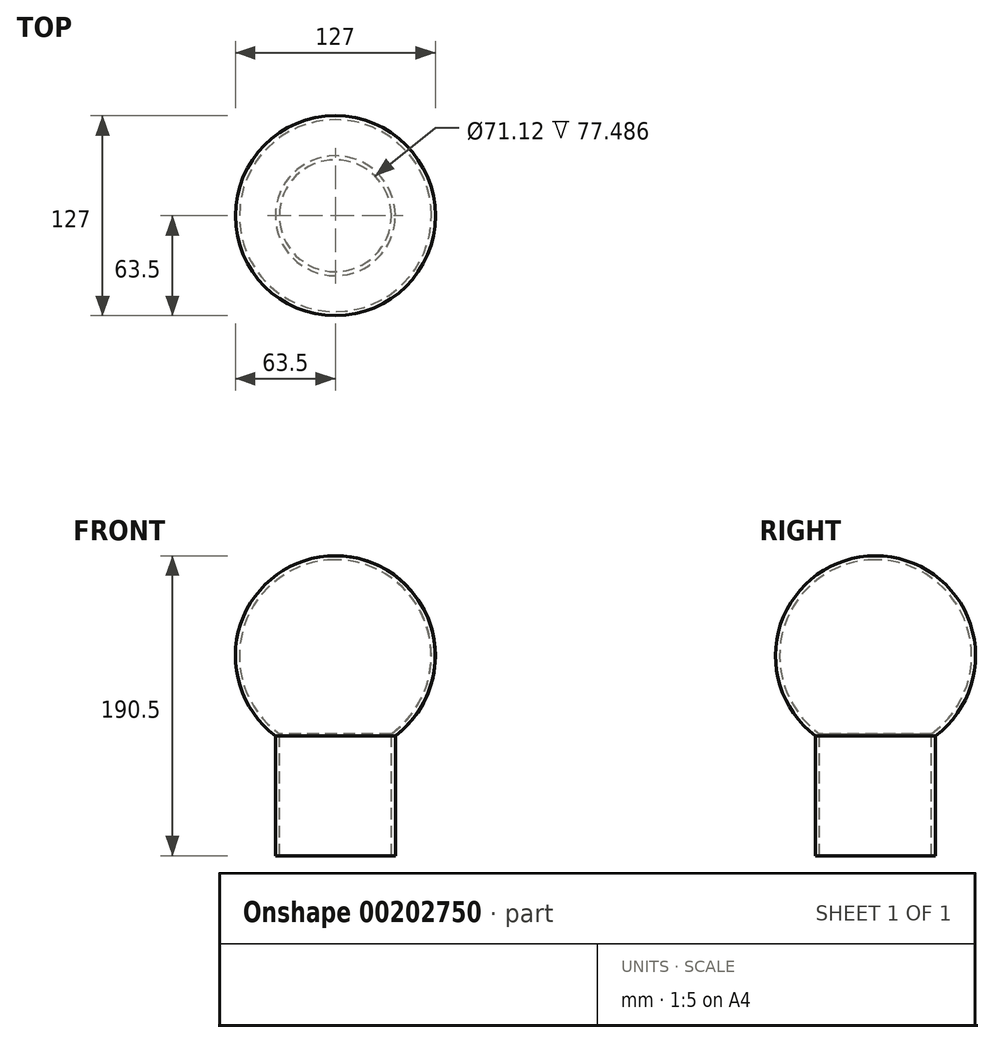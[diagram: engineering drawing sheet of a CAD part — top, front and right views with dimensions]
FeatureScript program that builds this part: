
annotation { "Feature Type Name" : "Feature", "Feature Type Description" : "" }
export const myFeature = defineFeature(function(context is Context, id is Id, definition is map)
    precondition{}
    {
        {
            var Q0;
            Q0=qCreatedBy(makeId("Top.planeOp"),FACE);
            var sketch = newSketch(context, id + "F0", { "sketchPlane" : qUnion([Q0])});
            skCircle(sketch, "E0", {"center": v(0, 0) * mm, "radius": 63.5 * mm});
            skPoint(sketch, "E1.orphan", {"position": v(-63.5, 0) * mm});
            skSolve(sketch);
        }
        {
            var Q0;
            Q0=makeQuery(id+"F0.imprint","IMPRINT",FACE,{"disambiguationData":[TD([[makeQuery(id+"F0.imprint","IMPRINT",EDGE,{"derivedFrom":sQuery(id+"F0.wireOp",EDGE,"E0")}),1.0]])]});
            extrude(context, id + "F1", {"entities" : qUnion([Q0]), "depth" : 127 * mm});
        }
        {
            var Q0;
            Q0=makeQuery(id+"F1.opExtrude","CAP_EDGE",EDGE,{"disambiguationData":[OSD([sQuery(id+"F0.wireOp",EDGE,"E0")])],"isStart":false});
            var Q1;
            Q1=makeQuery(id+"F1.opExtrude","CAP_EDGE",EDGE,{"disambiguationData":[OSD([sQuery(id+"F0.wireOp",EDGE,"E0")])],"isStart":true});
            fillet(context, id + "F2", {"entities" : qUnion([Q0, Q1]), "radius" : 63.5 * mm, "tangentPropagation" : true, "allowEdgeOverflow" : false});
        }
        {
            var Q0;
            Q0=makeQuery(id+"F0.imprint","IMPRINT",FACE,{"disambiguationData":[TD([[makeQuery(id+"F0.imprint","IMPRINT",EDGE,{"derivedFrom":sQuery(id+"F0.wireOp",EDGE,"E0")}),1.0]])]});
            extrude(context, id + "F3", {"entities" : qUnion([Q0]), "operationType" : NewBodyOperationType.REMOVE, "depth" : 12.7 * mm});
        }
        {
            var Q0;
            Q0=makeQuery(id+"F3.boolean.opBoolean","COPY",FACE,{"derivedFrom":makeQuery(id+"F3.opExtrude","CAP_FACE",FACE,{"disambiguationData":[OSD([sQuery(id+"F0.wireOp",EDGE,"E0")])],"isStart":false})});
            extrude(context, id + "F4", {"entities" : qUnion([Q0]), "operationType" : NewBodyOperationType.ADD, "depth" : 76.2 * mm});
        }
        {
            var Q0;
            Q0=makeQuery(id+"F4.opExtrude","CAP_FACE",FACE,{"disambiguationData":[OSD([sQuery(id+"F0.wireOp",EDGE,"E0")])],"isStart":false});
            shell(context, id + "F5", {"entities" : qUnion([Q0]), "thickness" : 2.54 * mm});
        }
    });
